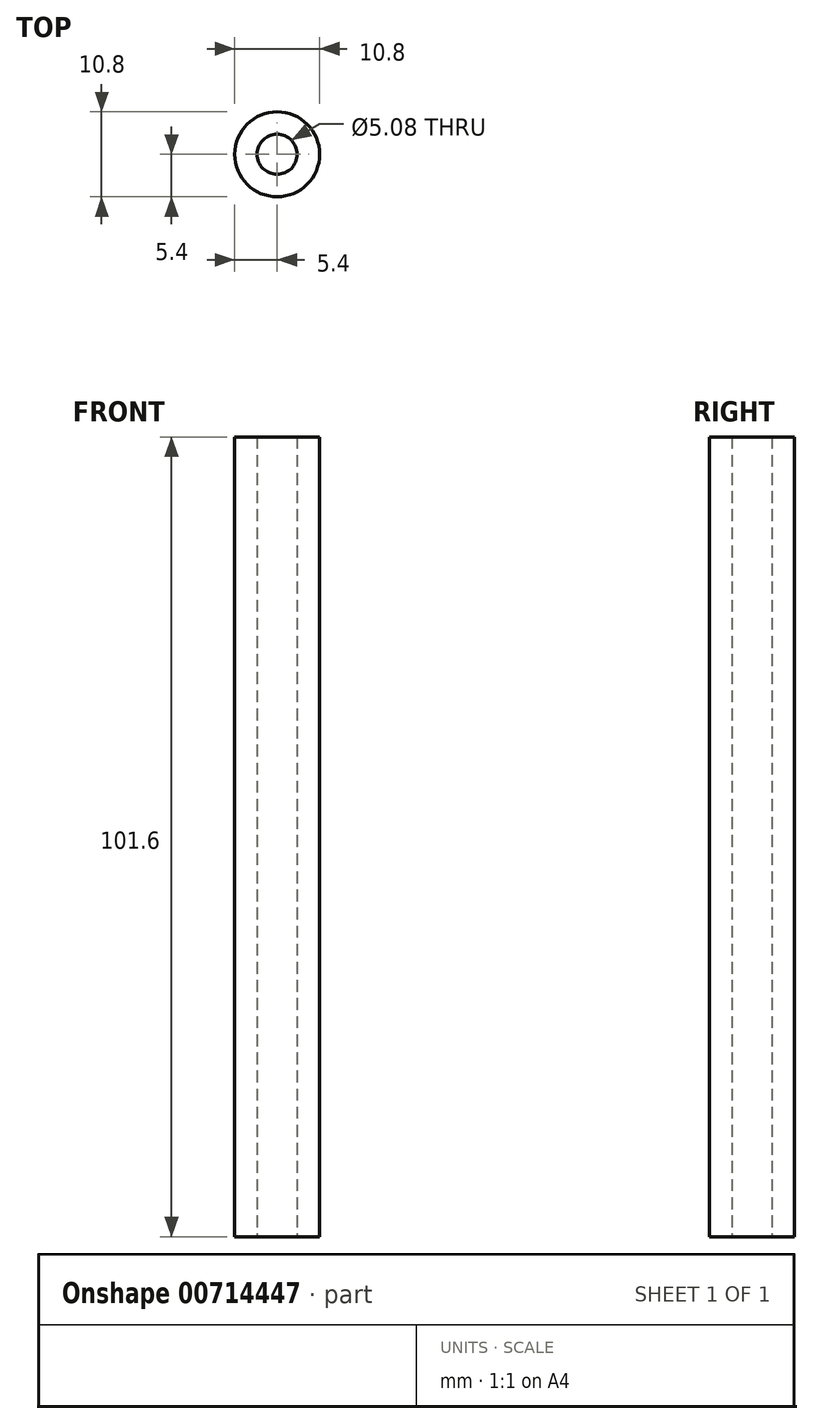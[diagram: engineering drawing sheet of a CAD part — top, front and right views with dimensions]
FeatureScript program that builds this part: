
annotation { "Feature Type Name" : "Feature", "Feature Type Description" : "" }
export const myFeature = defineFeature(function(context is Context, id is Id, definition is map)
    precondition{}
    {
        {
            var Q0;
            Q0=qCreatedBy(makeId("Top.planeOp"),FACE);
            var sketch = newSketch(context, id + "F0", { "sketchPlane" : qUnion([Q0])});
            skCircle(sketch, "E0", {"center": v(0, 0) * mm, "radius": 2.54 * mm});
            skCircle(sketch, "E1", {"center": v(0, 0) * mm, "radius": 5.4 * mm});
            skSolve(sketch);
        }
        {
            var Q0;
            Q0=makeQuery(id+"F0.imprint","IMPRINT",FACE,{"disambiguationData":[TD([[makeQuery(id+"F0.imprint","IMPRINT",EDGE,{"derivedFrom":sQuery(id+"F0.wireOp",EDGE,"E0")}),-1.0]])]});
            extrude(context, id + "F1", {"entities" : qUnion([Q0]), "depth" : 101.6 * mm});
        }
    });
